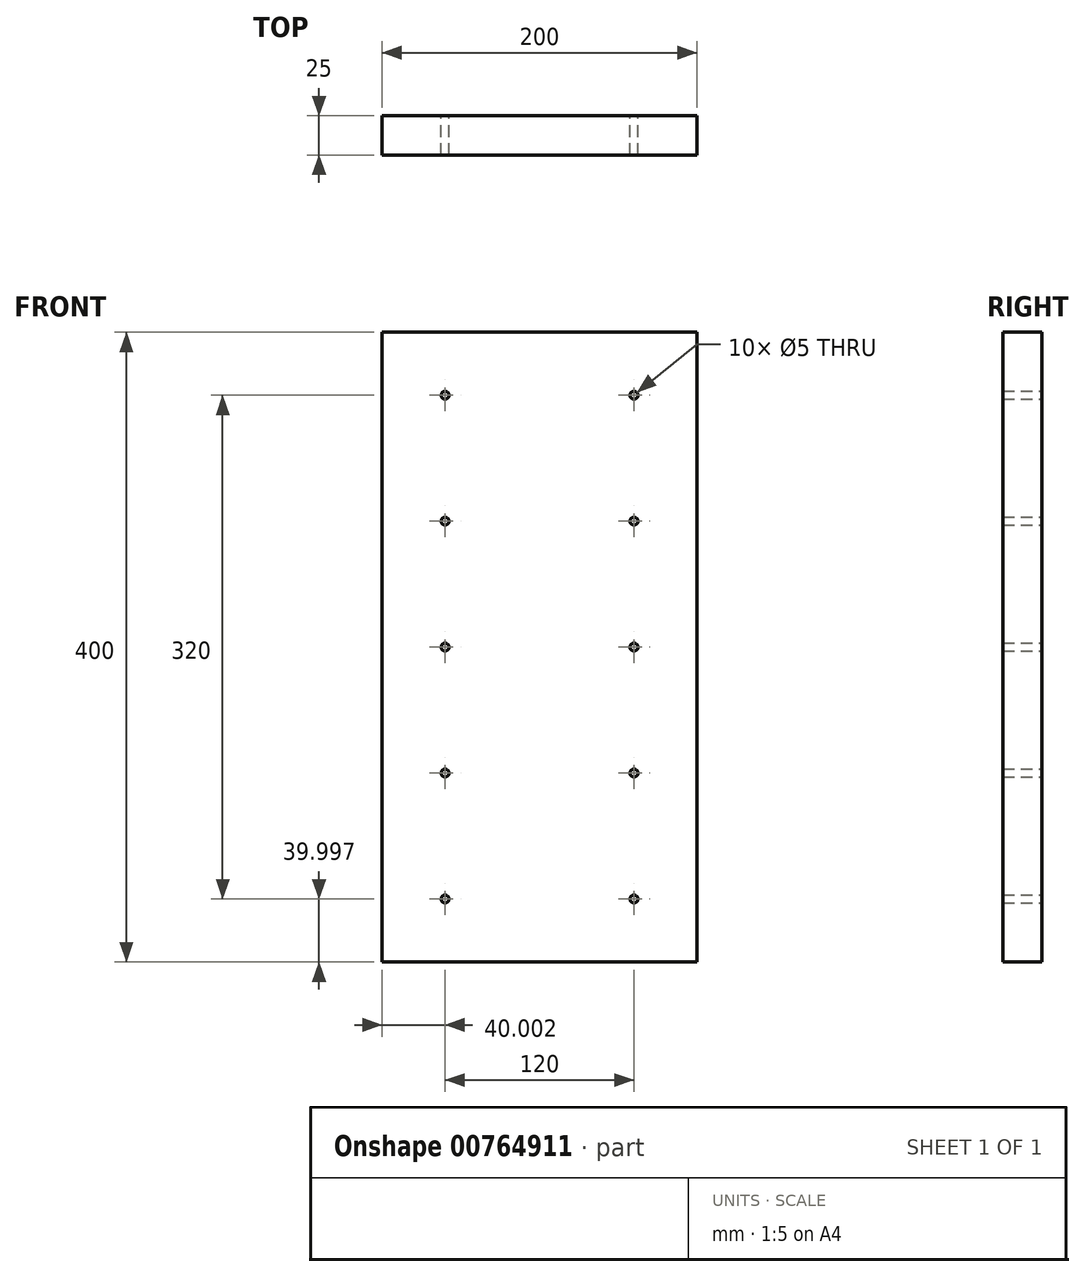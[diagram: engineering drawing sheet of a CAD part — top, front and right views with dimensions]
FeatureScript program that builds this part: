
annotation { "Feature Type Name" : "Feature", "Feature Type Description" : "" }
export const myFeature = defineFeature(function(context is Context, id is Id, definition is map)
    precondition{}
    {
        {
            var Q0;
            Q0=qCreatedBy(makeId("Front.planeOp"),FACE);
            var sketch = newSketch(context, id + "F0", { "sketchPlane" : qUnion([Q0])});
            skLineSegment(sketch, "E0.bottom", {"start": v(-89, 230.89) * mm, "end": v(111, 230.89) * mm});
            skLineSegment(sketch, "E0.top", {"start": v(-89, -169.11) * mm, "end": v(111, -169.11) * mm});
            skLineSegment(sketch, "E0.left", {"start": v(-89, 230.89) * mm, "end": v(-89, -169.11) * mm});
            skLineSegment(sketch, "E0.right", {"start": v(111, 230.89) * mm, "end": v(111, -169.11) * mm});
            skLineSegment(sketch, "E1", {"start": v(11, 230.89) * mm, "end": v(11, -169.11) * mm, "construction": true});
            skLineSegment(sketch, "E2", {"start": v(-89, 30.89) * mm, "end": v(111, 30.89) * mm, "construction": true});
            skLineSegment(sketch, "E3", {"start": v(-89, 190.89) * mm, "end": v(111, 190.89) * mm, "construction": true});
            skLineSegment(sketch, "E4", {"start": v(-89, 110.89) * mm, "end": v(111, 110.89) * mm, "construction": true});
            skCircle(sketch, "E5", {"center": v(-49, 190.89) * mm, "radius": 2.5 * mm});
            skCircle(sketch, "E6", {"center": v(71, 190.89) * mm, "radius": 2.5 * mm});
            skCircle(sketch, "E7", {"center": v(-49, 110.89) * mm, "radius": 2.5 * mm});
            skCircle(sketch, "E8", {"center": v(71, 110.89) * mm, "radius": 2.5 * mm});
            skCircle(sketch, "E9", {"center": v(-49, 30.89) * mm, "radius": 2.5 * mm});
            skCircle(sketch, "E10", {"center": v(71, 30.89) * mm, "radius": 2.5 * mm});
            skCircle(sketch, "E11.MirrorC", {"center": v(71, -129.11) * mm, "radius": 2.5 * mm});
            skCircle(sketch, "E12.MirrorC", {"center": v(-49, -49.11) * mm, "radius": 2.5 * mm});
            skCircle(sketch, "E13.MirrorC", {"center": v(71, -49.11) * mm, "radius": 2.5 * mm});
            skCircle(sketch, "E14.MirrorC", {"center": v(-49, -129.11) * mm, "radius": 2.5 * mm});
            skSolve(sketch);
        }
        {
            var Q0;
            Q0 = qSketchRegion(id + "F0", true);
            extrude(context, id + "F1", {"entities" : qUnion([Q0]), "depth" : 25 * mm, "offsetDistance" : 25 * mm});
        }
    });
